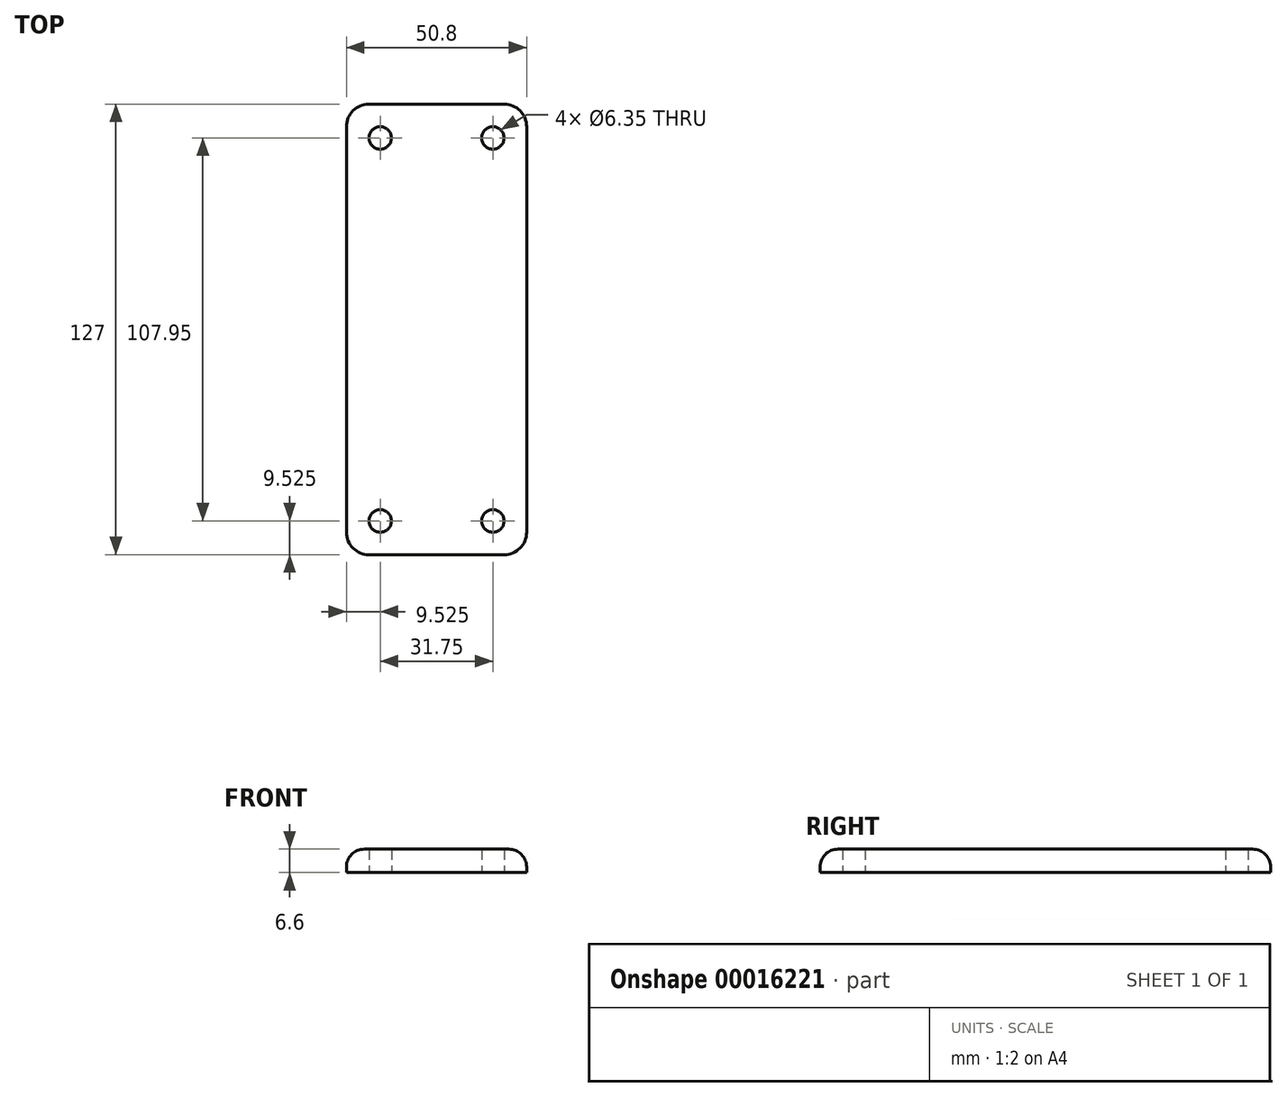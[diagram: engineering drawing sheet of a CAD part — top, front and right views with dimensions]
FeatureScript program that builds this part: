
annotation { "Feature Type Name" : "Feature", "Feature Type Description" : "" }
export const myFeature = defineFeature(function(context is Context, id is Id, definition is map)
    precondition{}
    {
        {
            var Q0;
            Q0=qCreatedBy(makeId("Top.planeOp"),FACE);
            var sketch = newSketch(context, id + "F0", { "sketchPlane" : qUnion([Q0])});
            skLineSegment(sketch, "E0.bottom", {"start": v(0, 0) * mm, "end": v(-25.4, 0) * mm});
            skLineSegment(sketch, "E0.top", {"start": v(0, 63.5) * mm, "end": v(-19.05, 63.5) * mm});
            skLineSegment(sketch, "E0.left", {"start": v(0, 0) * mm, "end": v(0, 63.5) * mm});
            skLineSegment(sketch, "E0.right", {"start": v(-25.4, 0) * mm, "end": v(-25.4, 57.15) * mm});
            skLineSegment(sketch, "E1", {"start": v(-25.4, 34.93) * mm, "end": v(0, 34.93) * mm});
            skCircle(sketch, "E2", {"center": v(-15.88, 53.97) * mm, "radius": 3.18 * mm});
            skPoint(sketch, "E3.visualSharp", {"position": v(-25.4, 63.5) * mm});
            skArc(sketch, "E3.filletArc", {"start": v(-19.05, 63.5) * mm, "mid": v(-23.54, 61.64) * mm, "end": v(-25.4, 57.15) * mm});
            skLineSegment(sketch, "E4.MirrorCS", {"start": v(0, 63.5) * mm, "end": v(19.05, 63.5) * mm});
            skArc(sketch, "E5.MirrorCS", {"start": v(19.05, 63.5) * mm, "mid": v(23.54, 61.64) * mm, "end": v(25.4, 57.15) * mm});
            skCircle(sketch, "E6.MirrorC", {"center": v(15.88, 53.97) * mm, "radius": 3.18 * mm});
            skLineSegment(sketch, "E7.MirrorCS", {"start": v(25.4, 0) * mm, "end": v(25.4, 57.15) * mm});
            skLineSegment(sketch, "E8.MirrorCS", {"start": v(25.4, 34.93) * mm, "end": v(0, 34.93) * mm});
            skLineSegment(sketch, "E9.MirrorCS", {"start": v(0, 0) * mm, "end": v(25.4, 0) * mm});
            skLineSegment(sketch, "E10.MirrorCS", {"start": v(25.4, 0) * mm, "end": v(25.4, -57.15) * mm});
            skLineSegment(sketch, "E11.MirrorCS", {"start": v(25.4, -34.93) * mm, "end": v(0, -34.93) * mm});
            skArc(sketch, "E12.MirrorCS", {"start": v(19.05, -63.5) * mm, "mid": v(23.54, -61.64) * mm, "end": v(25.4, -57.15) * mm});
            skLineSegment(sketch, "E13.MirrorCS", {"start": v(0, -63.5) * mm, "end": v(19.05, -63.5) * mm});
            skLineSegment(sketch, "E14.MirrorCS", {"start": v(0, -63.5) * mm, "end": v(-19.05, -63.5) * mm});
            skArc(sketch, "E15.MirrorCS", {"start": v(-19.05, -63.5) * mm, "mid": v(-23.54, -61.64) * mm, "end": v(-25.4, -57.15) * mm});
            skLineSegment(sketch, "E16.MirrorCS", {"start": v(-25.4, 0) * mm, "end": v(-25.4, -57.15) * mm});
            skCircle(sketch, "E17.MirrorC", {"center": v(-15.88, -53.97) * mm, "radius": 3.18 * mm});
            skCircle(sketch, "E18.MirrorC", {"center": v(15.88, -53.97) * mm, "radius": 3.18 * mm});
            skLineSegment(sketch, "E19.MirrorCS", {"start": v(-25.4, -34.93) * mm, "end": v(0, -34.93) * mm});
            skSolve(sketch);
        }
        {
            var Q0;
            {var subQ4=sQuery(id+"F0.wireOp",EDGE,"E0.top");Q0=makeQuery(id+"F0.imprint","IMPRINT",FACE,{"disambiguationData":[TD([[makeQuery(id+"F0.imprint","IMPRINT",EDGE,{"derivedFrom":subQ4}),1.0]])]});}
            var Q1;
            {var subQ2=sQuery(id+"F0.wireOp",EDGE,"E0.bottom");Q1=makeQuery(id+"F0.imprint","IMPRINT",FACE,{"disambiguationData":[TD([[makeQuery(id+"F0.imprint","IMPRINT",EDGE,{"derivedFrom":subQ2}),-1.0]])]});}
            var Q2;
            {var subQ1=sQuery(id+"F0.wireOp",EDGE,"E8.MirrorCS");Q2=makeQuery(id+"F0.imprint","IMPRINT",FACE,{"disambiguationData":[TD([[makeQuery(id+"F0.imprint","IMPRINT",EDGE,{"derivedFrom":subQ1}),1.0]])]});}
            var Q3;
            {var subQ3=sQuery(id+"F0.wireOp",EDGE,"E4.MirrorCS");Q3=makeQuery(id+"F0.imprint","IMPRINT",FACE,{"disambiguationData":[TD([[makeQuery(id+"F0.imprint","IMPRINT",EDGE,{"derivedFrom":subQ3}),-1.0]])]});}
            var Q4;
            {var subQ5=sQuery(id+"F0.wireOp",EDGE,"E11.MirrorCS");Q4=makeQuery(id+"F0.imprint","IMPRINT",FACE,{"disambiguationData":[TD([[makeQuery(id+"F0.imprint","IMPRINT",EDGE,{"derivedFrom":subQ5}),1.0]])]});}
            var Q5;
            {var subQ2=sQuery(id+"F0.wireOp",EDGE,"E0.bottom");Q5=makeQuery(id+"F0.imprint","IMPRINT",FACE,{"disambiguationData":[TD([[makeQuery(id+"F0.imprint","IMPRINT",EDGE,{"derivedFrom":subQ2}),1.0]])]});}
            extrude(context, id + "F1", {"entities" : qUnion([Q0, Q1, Q2, Q3, Q4, Q5]), "depth" : 6.6 * mm});
        }
        {
            var Q0;
            Q0=makeQuery(id+"F1.opExtrude","CAP_EDGE",EDGE,{"disambiguationData":[OSD([sQuery(id+"F0.wireOp",EDGE,"E0.right"),sQuery(id+"F0.wireOp",EDGE,"E16.MirrorCS")])],"isStart":false});
            fillet(context, id + "F2", {"entities" : qUnion([Q0]), "radius" : 5.08 * mm, "tangentPropagation" : true, "allowEdgeOverflow" : false});
        }
    });
